# Revit family: LAMP_FIL 70 OPAL RECESSED
name_source: partatom
category: Luminarias
revit_build: Autodesk Revit 2015 (Build: 20140606_1530(x64)
units: mm (PartAtom-declared; Revit-internal decimal feet)

## types (16) — shared parameters
CRI = 80
Cambio de temperatura de color de luz atenuada = <Ninguno>
Comentarios de tipo = Availability of switching between accessories through visibility parameters when placed in a project.
Filtro de color = 16777215
Gear = Electronic
IFC Clasificación = Light Fixture
Installation instructions = https://www.lamp.es
Insulation class = I
Last update = 12/08/2020
Luminaire type = Indoor - Modular System
Lámpara = LED MID-POWER
MacAdam = 3
Manufacturer URL = http://www.lamp.es
Manufacturer country = Spain
Material Difusor = LAMP_PC Difusor Opal Fil
Model explanation = Availability of switching between accessories through visibility parameters when placed in a project.
Power Supply = 220-240V 50-60Hz
Product URL = https://www.lamp.es
Product datasheet = https://www.lamp.es
Protection rating = IP42, IK06
Type = MID POWER PHILIPS
Ángulo de inclinación = 90,00°

## per-type parameters (varying)
| type | Archivo de red fotométrica | Descripción | Dimensions | Efficacy | Fabricante | Finish | IEE | LED Lifetime | Longitud | Longitud de línea de emisión | Manufacturer name | Material Perfil | Modelo | Plum | Power | Product code | Recessed dimensions | UniClass 1.4 Code | UniClass 2.0 Code | Weight |
| 1162MM 2600LM 3000K WHITE | 4741690.IES | FIL 70 OPAL REC 2600 WW WH. | 1162 x 89 x 70 mm | 104 lm/W | LAMP | Matt white | A+ | 60.000 L80 B10 | 1162 mm  [stored 3.81234 ft] | 1162 mm  [stored 3.81234 ft] | LAMP | LAMP_Aluminio Perfil Fil BL | F71RE120LOOP830NW | 19 W | 17 W | F71RE120LOOP830NW | 1174 x 78 x 85 mm | F71RE120LOOP830NW | F71RE120LOOP830NW | 2,66 kg |
| 1162MM 2600LM 3000K GREY | 4741693.IES | FIL 70 OPAL REC 2600 WW GR. | 1162 x 89 x 70 mm | 104 lm/W | LAMP | Gloss grey | A+ | 60.000 L80 B10 | 1162 mm  [stored 3.81234 ft] | 1162 mm  [stored 3.81234 ft] | LAMP | LAMP_Aluminio Perfil Fil GR | F71RE120LOOP830NG | 19 W | 17 W | F71RE120LOOP830NG | 1174 x 78 x 85 mm | F71RE120LOOP830NG | F71RE120LOOP830NG | 2,66 kg |
| 1162MM 2600LM 4000K WHITE | 4740690.IES | FIL 70 OPAL REC 2600 NW WH. | 1162 x 89 x 70 mm | 112 lm/W | LAMP | Matt white | A++ | 60.000 L80 B10 | 1162 mm  [stored 3.81234 ft] | 1162 mm  [stored 3.81234 ft] | LAMP | LAMP_Aluminio Perfil Fil BL | F71RE120LOOP840NW | 19 W | 17 W | F71RE120LOOP840NW | 1174 x 78 x 85 mm | F71RE120LOOP840NW | F71RE120LOOP840NW | 2,66 kg |
| 1162MM 2600LM 4000K GREY | 4740693.IES | FIL 70 OPAL REC 2600 NW GR. | 1162 x 89 x 70 mm | 112 lm/W | LAMP | Gloss grey | A++ | 60.000 L80 B10 | 1162 mm  [stored 3.81234 ft] | 1162 mm  [stored 3.81234 ft] | LAMP | LAMP_Aluminio Perfil Fil GR | F71RE120LOOP840NG | 19 W | 17 W | F71RE120LOOP840NG | 1174 x 78 x 85 mm | F71RE120LOOP840NG | F71RE120LOOP840NG | 2,66 kg |
| 1162MM 4400LM 3000K WHITE | 4741590.IES | FIL 70 OPAL REC 4400 WW WH. | 1162 x 89 x 70 mm | 110 lm/W | LAMP | Matt white | A++ | 60.000 L80 B10 | 1162 mm  [stored 3.81234 ft] | 1162 mm  [stored 3.81234 ft] | LAMP | LAMP_Aluminio Perfil Fil BL | F71RE120HOOP830NW | 31 W | 28 W | F71RE120HOOP830NW | 1174 x 78 x 85 mm | F71RE120HOOP830NW | F71RE120HOOP830NW | 2,66 kg |
| 1162MM 4400LM 3000K GREY | 4741593.IES | FIL 70 OPAL REC 4400 WW GR. | 1162 x 89 x 70 mm | 110 lm/W | LAMP | Gloss grey | A++ | 60.000 L80 B10 | 1162 mm  [stored 3.81234 ft] | 1162 mm  [stored 3.81234 ft] | LAMP | LAMP_Aluminio Perfil Fil GR | F71RE120HOOP830NG | 31 W | 28 W | F71RE120HOOP830NG | 1174 x 78 x 85 mm | F71RE120HOOP830NG | F71RE120HOOP830NG | 2,66 kg |
| 1162MM 4400LM 4000K WHITE | 4740590.IES | FIL 50 OPAL REC 4400 NW WH. | 1162 x 89 x 70 mm | 116 lm/W | LAMP | Matt white | A++ | 60.000 L80 B10 | 1162 mm  [stored 3.81234 ft] | 1162 mm  [stored 3.81234 ft] | LAMP | LAMP_Aluminio Perfil Fil BL | F71RE120HOOP840NW | 31 W | 28 W | F71RE120HOOP840NW | 1174 x 78 x 85 mm | F71RE120HOOP840NW | F71RE120HOOP840NW | 2,67 kg |
| 1162MM 4400LM 4000K GREY | 4740593.IES | FIL 70 OPAL REC 4400 NW GR. | 1162 x 89 x 70 mm | 116 lm/W | LAMP | Gloss grey | A++ | 60.000 L80 B10 | 1162 mm  [stored 3.81234 ft] | 1162 mm  [stored 3.81234 ft] | LAMP | LAMP_Aluminio Perfil Fil GR | F71RE120HOOP840NG | 31 W | 28 W | F71RE120HOOP840NG | 1174 x 78 x 85 mm | F71RE120HOOP840NG | F71RE120HOOP840NG | 2,67 kg |
| 1743MM 3900LM 3000K WHITE | 4741700.IES | FIL 70 OPAL REC 3900 WW WH. | 1743 x 89 x 70 mm | 101 lm/W | LAMP | Matt white | A+ | 50.000 L80 B10 | 1743 mm  [stored 5.7185 ft] | 1743 mm  [stored 5.7185 ft] | LAMP | LAMP_Aluminio Perfil Fil BL | F71RE170LOOP830NW | 30 W | 25 W | F71RE170LOOP830NW | 1755 x 78 x 85 mm | F71RE170LOOP830NW | F71RE170LOOP830NW | 4,27 kg |
| 1743MM 3900LM 3000K GREY | 4741703.IES | FIL 70 OPAL REC 3900 WW GR. | 1743 x 89 x 70 mm | 101 lm/W | LAMP | Gloss grey | A+ | 50.000 L80 B10 | 1743 mm  [stored 5.7185 ft] | 1743 mm  [stored 5.7185 ft] | LAMP | LAMP_Aluminio Perfil Fil GR | F71RE170LOOP830NG | 30 W | 25 W | F71RE170LOOP830NG | 1755 x 78 x 85 mm | F71RE170LOOP830NG | F71RE170LOOP830NG | 4,27 kg |
| 1743MM 3900LM 4000K WHITE | 4740700.IES | FIL 50 OPAL REC 3900 NW WH. | 1743 x 89 x 70 mm | 108 lm/W | LAMP | Matt white | A++ | 50.000 L80 B10 | 1743 mm  [stored 5.7185 ft] | 1743 mm  [stored 5.7185 ft] | LAMP | LAMP_Aluminio Perfil Fil BL | F71RE170LOOP840NW | 30 W | 25 W | F71RE170LOOP840NW | 1755 x 78 x 85 mm | F71RE170LOOP840NW | F71RE170LOOP840NW | 4,27 kg |
| 1743MM 3900LM 4000K GREY | 4740703.IES | FIL 70 OPAL REC 3900 NW GR. | 1743 x 89 x 70 mm | 108 lm/W | Lamp | Gloss grey | A++ | 50.000 L80 B10 | 1743 mm  [stored 5.7185 ft] | 1743 mm  [stored 5.7185 ft] | Lamp | LAMP_Aluminio Perfil Fil GR | F71RE170LOOP840NG | 30 W | 25 W | F71RE170LOOP840NG | 1755 x 78 x 85 mm | F71RE170LOOP840NG | F71RE170LOOP840NG | 4,27 kg |
| 1743MM 6600LM 3000K WHITE | 4741600.IES | FIL 70 OPAL REC 6600 WW WH. | 1743 x 89 x 70 mm | 110 lm/W | LAMP | Matt white | A++ | 50.000 L80 B10 | 1743 mm  [stored 5.7185 ft] | 1743 mm  [stored 5.7185 ft] | LAMP | LAMP_Aluminio Perfil Fil BL | F71RE170HOOP830NW | 46 W | 41 W | F71RE170HOOP830NW | 1755 x 78 x 85 mm | F71RE170HOOP830NW | F71RE170HOOP830NW | 4,28 kg |
| 1743MM 6600LM 3000K GREY | 4741603.IES | FIL 50 OPAL REC 6600 WW GR. | 1743 x 89 x 70 mm | 110 lm/W | LAMP | Gloss grey | A++ | 50.000 L80 B10 | 1743 mm  [stored 5.7185 ft] | 1743 mm  [stored 5.7185 ft] | LAMP | LAMP_Aluminio Perfil Fil GR | F71RE170HOOP830NG | 46 W | 41 W | F71RE170HOOP830NG | 1755 x 78 x 85 mm | F71RE170HOOP830NG | F71RE170HOOP830NG | 4,28 kg |
| 1743MM 6600LM 4000K WHITE | 4740600.IES | FIL 70 OPAL REC 6600 NW WH. | 1743 x 89 x 70 mm | 116 lm/W | LAMP | Matt white | A++ | 50.000 L80 B10 | 1743 mm  [stored 5.7185 ft] | 1743 mm  [stored 5.7185 ft] | LAMP | LAMP_Aluminio Perfil Fil BL | F71RE170HOOP840NW | 46 W | 41 W | F71RE170HOOP840NW | 1755 x 78 x 85 mm | F71RE170HOOP840NW | F71RE170HOOP840NW | 4,28 kg |
| 1743MM 6600LM 4000K GREY | 4740603.IES | FIL 50 OPAL REC 6600 NW GR. | 1743 x 89 x 70 mm | 116 lm/W | LAMP | Gloss grey | A++ | 50.000 L80 B10 | 1743 mm  [stored 5.7185 ft] | 1743 mm  [stored 5.7185 ft] | LAMP | LAMP_Aluminio Perfil Fil GR | F71RE170HOOP840NG | 46 W | 41 W | F71RE170HOOP840NG | 1755 x 78 x 85 mm | F71RE170HOOP840NG | F71RE170HOOP840NG | 4,28 kg |

note: [stored X ft] marks values corroborated as IEEE doubles in the binary element streams (Revit-internal decimal feet)

## geometry (parser evidence)
native form markers: Blend x10
no freeform markers — native parametric forms only
